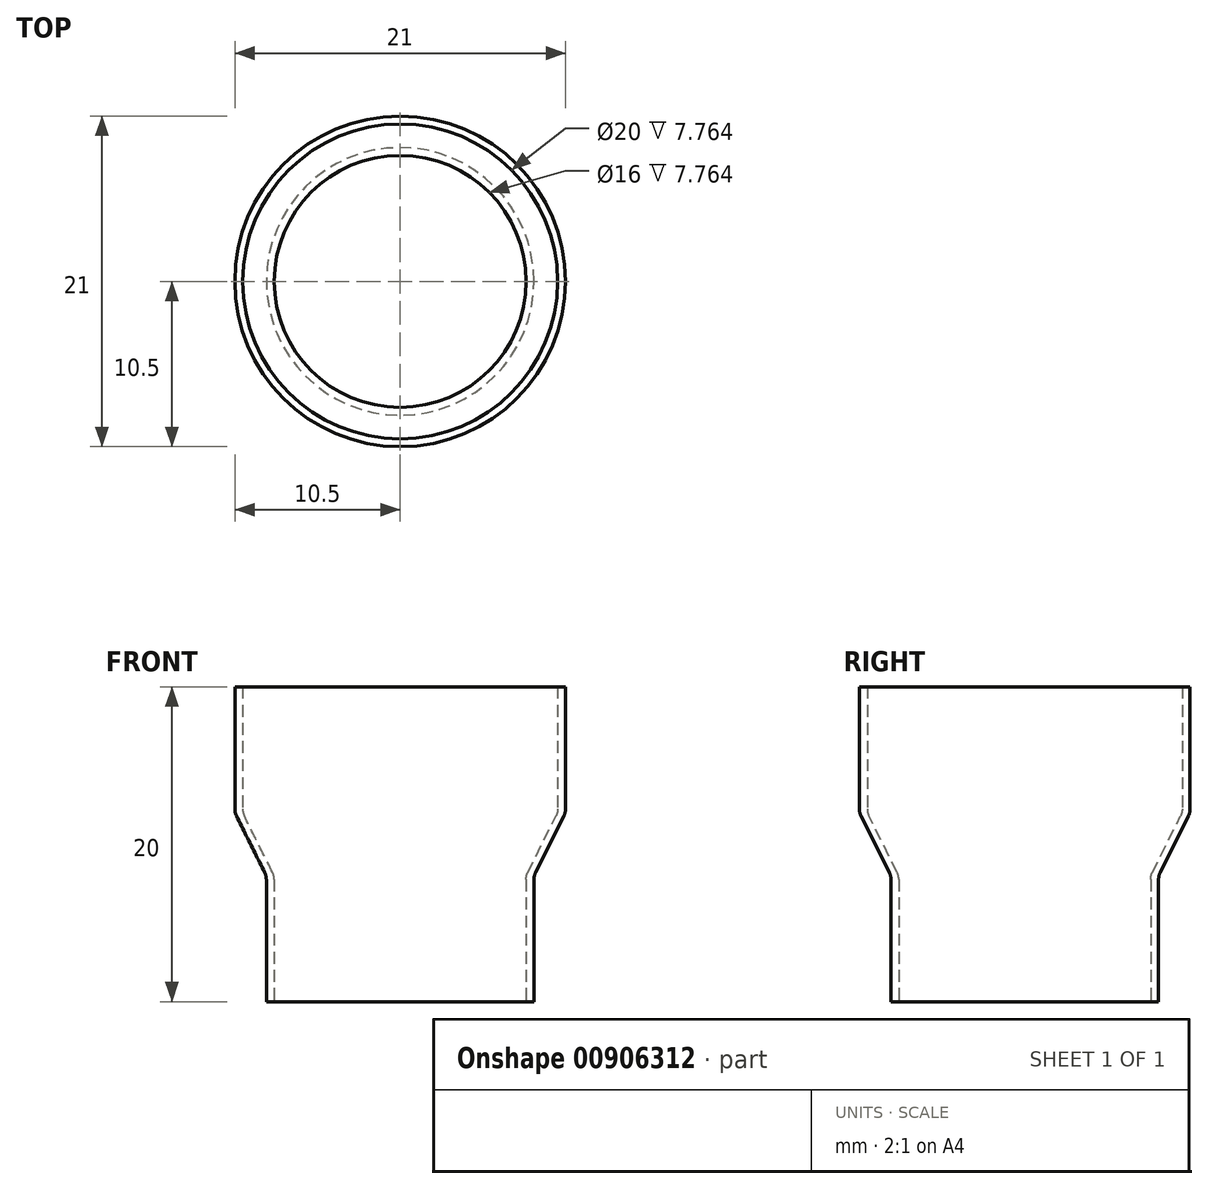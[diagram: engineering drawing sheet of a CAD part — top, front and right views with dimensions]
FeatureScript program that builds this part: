
annotation { "Feature Type Name" : "Feature", "Feature Type Description" : "" }
export const myFeature = defineFeature(function(context is Context, id is Id, definition is map)
    precondition{}
    {
        {
            var Q0;
            Q0=qCreatedBy(makeId("Top.planeOp"),FACE);
            var sketch = newSketch(context, id + "F0", { "sketchPlane" : qUnion([Q0])});
            skCircle(sketch, "E0", {"center": v(0, 0) * mm, "radius": 8.5 * mm});
            skCircle(sketch, "E1", {"center": v(0, 0) * mm, "radius": 8 * mm});
            skSolve(sketch);
        }
        {
            var Q0;
            Q0=qCreatedBy(makeId("Front.planeOp"),FACE);
            var sketch = newSketch(context, id + "F1", { "sketchPlane" : qUnion([Q0])});
            skLineSegment(sketch, "E2", {"start": v(8, 0) * mm, "end": v(8, 7.76) * mm});
            skLineSegment(sketch, "E3", {"start": v(10, 20) * mm, "end": v(10, 12.24) * mm});
            skLineSegment(sketch, "E4", {"start": v(10, 20) * mm, "end": v(10.5, 20) * mm});
            skLineSegment(sketch, "E5", {"start": v(10.5, 20) * mm, "end": v(10.5, 12.24) * mm});
            skLineSegment(sketch, "E6", {"start": v(8, 0) * mm, "end": v(8.5, 0) * mm});
            skLineSegment(sketch, "E7", {"start": v(8.5, 0) * mm, "end": v(8.5, 7.76) * mm});
            skLineSegment(sketch, "E8", {"start": v(8.1, 8.21) * mm, "end": v(9.9, 11.79) * mm});
            skLineSegment(sketch, "E9", {"start": v(8.6, 8.21) * mm, "end": v(10.4, 11.79) * mm});
            skPoint(sketch, "E10.visualSharp", {"position": v(8.5, 8) * mm});
            skArc(sketch, "E10.filletArc", {"start": v(8.6, 8.21) * mm, "mid": v(8.53, 8) * mm, "end": v(8.5, 7.76) * mm});
            skPoint(sketch, "E11.visualSharp", {"position": v(10.5, 12) * mm});
            skArc(sketch, "E11.filletArc", {"start": v(10.4, 11.79) * mm, "mid": v(10.47, 12) * mm, "end": v(10.5, 12.24) * mm});
            skPoint(sketch, "E12.visualSharp", {"position": v(10, 12) * mm});
            skArc(sketch, "E12.filletArc", {"start": v(9.9, 11.79) * mm, "mid": v(9.97, 12) * mm, "end": v(10, 12.24) * mm});
            skPoint(sketch, "E13.visualSharp", {"position": v(8, 8) * mm});
            skArc(sketch, "E13.filletArc", {"start": v(8.1, 8.21) * mm, "mid": v(8.03, 8) * mm, "end": v(8, 7.76) * mm});
            skSolve(sketch);
        }
        {
            var Q0;
            Q0=makeQuery(id+"F1.imprint","IMPRINT",FACE,{"disambiguationData":[TD([[makeQuery(id+"F1.imprint","IMPRINT",EDGE,{"derivedFrom":sQuery(id+"F1.wireOp",EDGE,"E2")}),-1.0]])]});
            var Q1;
            Q1=sQuery(id+"F0.wireOp",EDGE,"E1");
            revolve(context, id + "F2", {"surfaceOperationType" : NewSurfaceOperationType.NEW, "entities" : qUnion([Q0]), "axis" : qUnion([Q1]), "revolveType" : RevolveType.FULL});
        }
    });
